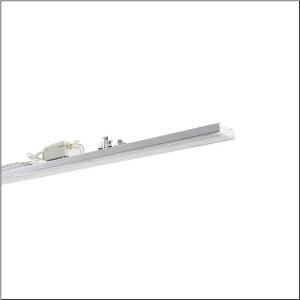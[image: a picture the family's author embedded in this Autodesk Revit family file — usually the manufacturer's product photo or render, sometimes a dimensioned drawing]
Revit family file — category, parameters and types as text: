
# Revit family: licross_r__21_recessed_mo_52te12dn4axg_78cf
name_source: partatom
category: Lighting Fixtures
units: mm (PartAtom-declared; Revit-internal decimal feet)

## family parameters
Cut with Voids When Loaded = No
Host = Face
Light Source = No
Part Type = Normal
Room Calculation Point = No
Round Connector Dimension = Use Diameter
Shared = No

## types (1)
- --- (1 x LED, 10280 lm, 58 W, 4000K)
    Apparent Load = 58 VA
    CIE Flux Codes = 72 92 99 100 100
    Color Rendering = 80
    Color Temperature = 4000K
    Default Elevation = 1800 mm
    Description = Licross® 21 Recessed MO, luminaire insert, of sheet steel, galvanised, coil coated, white, length: 1.500mm, width: 66mm, height: 67mm, LED rated luminous flux: 10.280lm, light colour: 840, control gear: DALI 2, with plug, 5-pole, with phase selection, mains connection: 220..240V, AC, 50/60Hz, rated input power: 58W, halogen-free wiring, primary optical cover: cover, of PMMA, light emission: direct distribution, primary light characteristic: symmetric, protection rating (complete): IP54, insulation class (complete): insulation class I (protective earthing), certification: CE, ENEC, VDE, UKCA, protection symbol: D if used in an environment with non-conductive dust loads with corresponding accessories, impact resistance: IK06, permissible ambient temperature for indoor applications: -25..+35°C, corresponds to IFS (International Featured Standards) requirements for safety and quality in the food industry, reducing of maximum allowable ambient temperature of 5°C with ceiling mounting, LABS conformity tested according to VDMA 24364:2018-05, packaging unit: 1 piece
    Height = 58 mm
    Lamp = 1 x LED
    Lamp Light Flux = 10280 lm
    Lamp Power = 58 W
    Lamp count = 1
    Length = 1500 mm
    Luminous efficacy = 177 lm/W
    Manufacturer = Siteco
    ModVariant = No
    Model = 52TE12DN4AXG
    Mounting Place = Ceiling
    Mounting Type = Pendant
    Number of Poles = 1
    OnlyDefault = Yes
    Power Factor = 1
    Product Name = Licross® 21 Recessed MO
    Product group = luminaire insert
    ProductGroupID = 901
    Protection Class = Protection class I
    Protection Degree = IP 54
    RLX_Detail_Level = 1
    RLX_Emergency_Light_Flux = 0 lm
    RLX_Emergency_Type = 0
    RLX_Emergency_Type_DB = No
    RlxData = <blob elided: 24641 chars, md5=81de9544>
    Socket = socket
    Standby Power = 0 W
    System Light Flux = 10280 lm
    System Power = 58 W
    Type Comments = factory setting: luminous flux: 100 % | dim-lin: 254 | 390 mA
    Type Image = l_1296930.jpg
    URL = http://relux.com
    VarID = @adj_057667
    Voltage = 0 V
    Weight = 0.00 kg
    Width = 66 mm

## geometry (parser evidence)
native form markers: Blend x4, Sweep x9
no freeform markers — native parametric forms only
